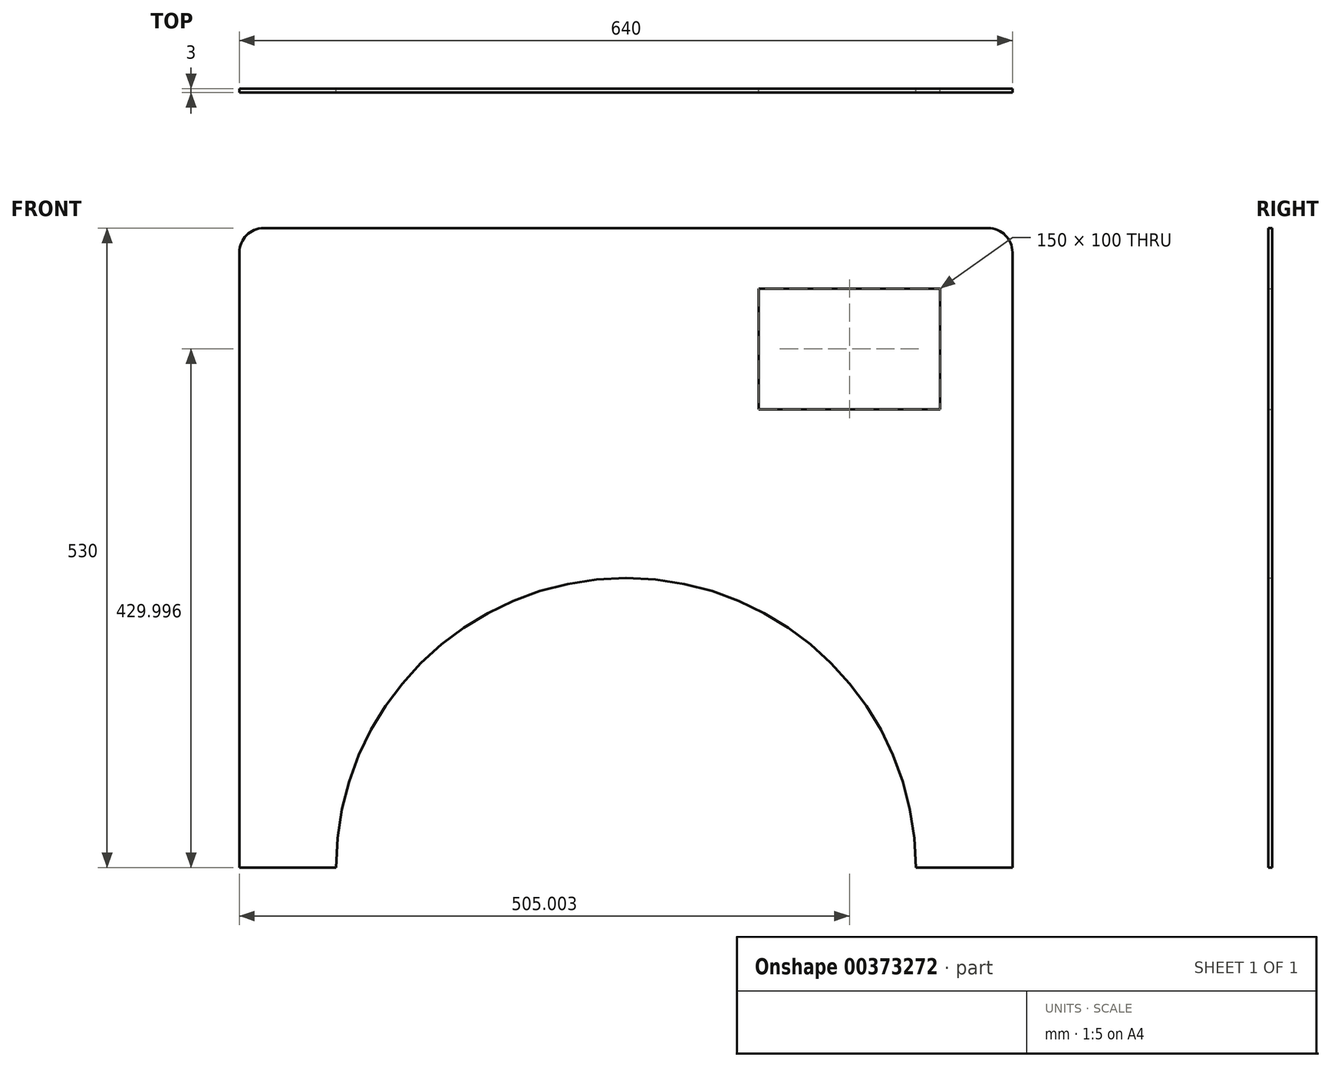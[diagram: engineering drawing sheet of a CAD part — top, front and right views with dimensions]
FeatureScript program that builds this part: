
annotation { "Feature Type Name" : "Feature", "Feature Type Description" : "" }
export const myFeature = defineFeature(function(context is Context, id is Id, definition is map)
    precondition{}
    {
        {
            var Q0;
            Q0=qCreatedBy(makeId("Front.planeOp"),FACE);
            var sketch = newSketch(context, id + "F0", { "sketchPlane" : qUnion([Q0])});
            skLineSegment(sketch, "E0.bottom", {"start": v(-356.89, 314.54) * mm, "end": v(243.11, 314.54) * mm});
            skLineSegment(sketch, "E0.top", {"start": v(-376.89, -215.46) * mm, "end": v(-296.89, -215.46) * mm});
            skLineSegment(sketch, "E0.left", {"start": v(-376.89, 294.54) * mm, "end": v(-376.89, -215.46) * mm});
            skLineSegment(sketch, "E0.right", {"start": v(263.11, 294.54) * mm, "end": v(263.11, -215.46) * mm});
            skArc(sketch, "E1", {"start": v(183.11, -215.46) * mm, "mid": v(-56.89, 24.54) * mm, "end": v(-296.89, -215.46) * mm});
            skLineSegment(sketch, "E2.trimOffspring", {"start": v(183.11, -215.46) * mm, "end": v(263.11, -215.46) * mm});
            skLineSegment(sketch, "E3.bottom", {"start": v(53.11, 264.54) * mm, "end": v(203.11, 264.54) * mm});
            skLineSegment(sketch, "E3.top", {"start": v(53.11, 164.54) * mm, "end": v(203.11, 164.54) * mm});
            skLineSegment(sketch, "E3.left", {"start": v(53.11, 264.54) * mm, "end": v(53.11, 164.54) * mm});
            skLineSegment(sketch, "E3.right", {"start": v(203.11, 264.54) * mm, "end": v(203.11, 164.54) * mm});
            skPoint(sketch, "E4.visualSharp", {"position": v(-376.89, 314.54) * mm});
            skArc(sketch, "E4.filletArc", {"start": v(-356.89, 314.54) * mm, "mid": v(-371.03, 308.68) * mm, "end": v(-376.89, 294.54) * mm});
            skPoint(sketch, "E5.visualSharp", {"position": v(263.11, 314.54) * mm});
            skArc(sketch, "E5.filletArc", {"start": v(263.11, 294.54) * mm, "mid": v(257.25, 308.68) * mm, "end": v(243.11, 314.54) * mm});
            skSolve(sketch);
        }
        {
            var Q0;
            Q0 = qSketchRegion(id + "F0", true);
            extrude(context, id + "F1", {"entities" : qUnion([Q0]), "depth" : 3 * mm});
        }
    });
